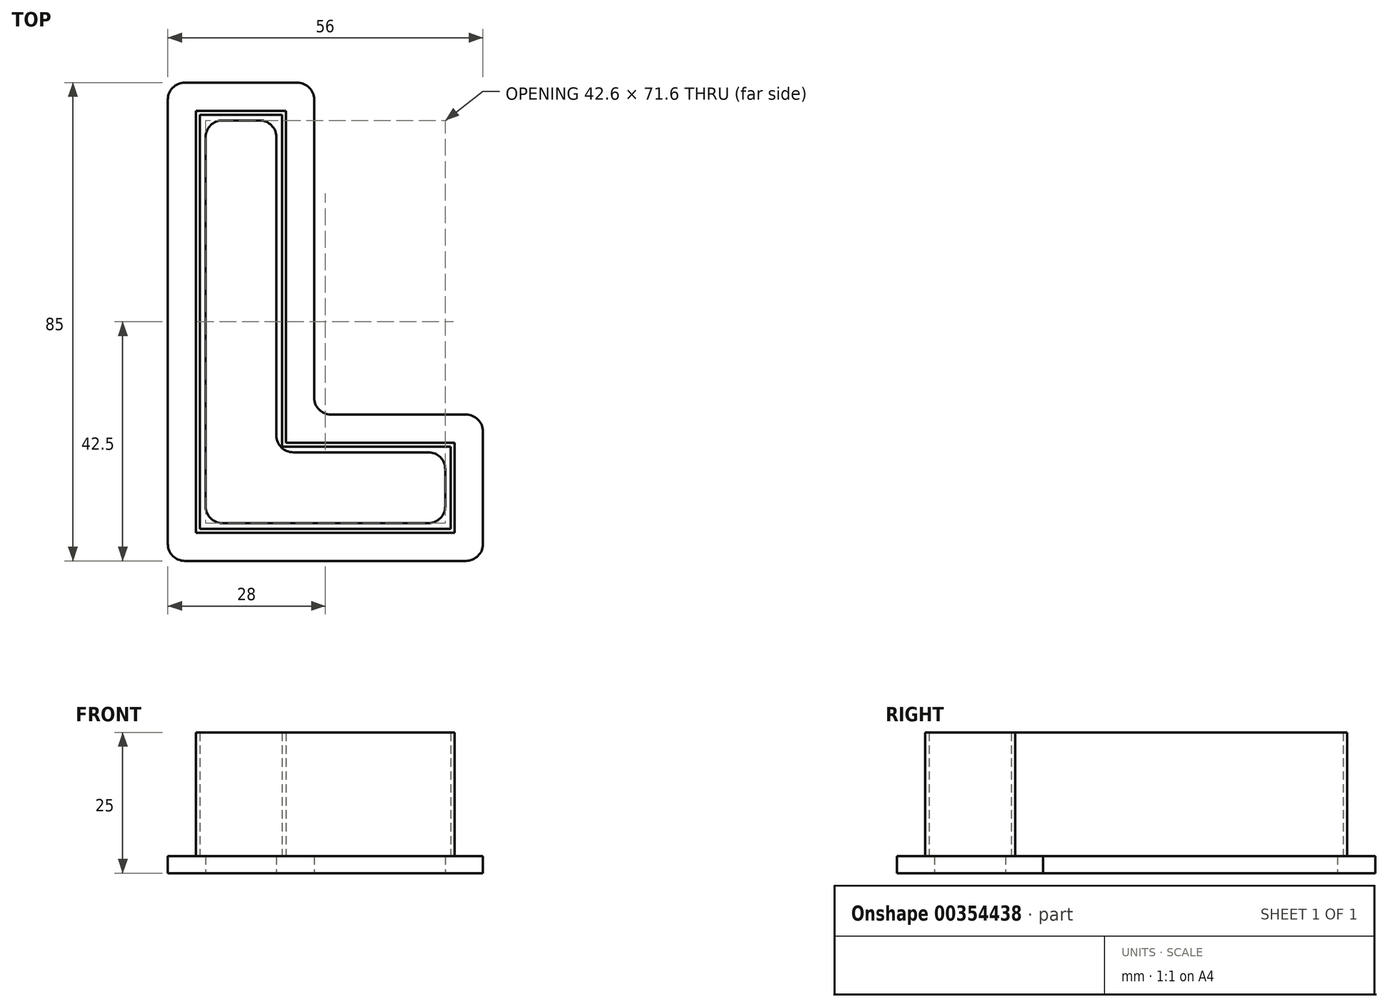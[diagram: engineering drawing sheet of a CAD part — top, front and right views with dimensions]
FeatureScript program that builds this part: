
annotation { "Feature Type Name" : "Feature", "Feature Type Description" : "" }
export const myFeature = defineFeature(function(context is Context, id is Id, definition is map)
    precondition{}
    {
        {
            var Q0;
            Q0=qCreatedBy(makeId("Top.planeOp"),FACE);
            var sketch = newSketch(context, id + "F0", { "sketchPlane" : qUnion([Q0])});
            skLineSegment(sketch, "E0", {"start": v(0, 0) * mm, "end": v(30, 0) * mm});
            skLineSegment(sketch, "E1", {"start": v(30, 0) * mm, "end": v(30, -16) * mm});
            skLineSegment(sketch, "E2", {"start": v(30, -16) * mm, "end": v(-16, -16) * mm});
            skLineSegment(sketch, "E3", {"start": v(-16, -16) * mm, "end": v(-16, 59) * mm});
            skLineSegment(sketch, "E4", {"start": v(-16, 59) * mm, "end": v(0, 59) * mm});
            skLineSegment(sketch, "E5", {"start": v(0, 59) * mm, "end": v(0, 0) * mm});
            skLineSegment(sketch, "E6.0", {"start": v(35, 5) * mm, "end": v(35, -21) * mm});
            skLineSegment(sketch, "E6.1", {"start": v(-21, -21) * mm, "end": v(-21, 64) * mm});
            skLineSegment(sketch, "E6.2", {"start": v(-21, 64) * mm, "end": v(5, 64) * mm});
            skLineSegment(sketch, "E6.3", {"start": v(35, -21) * mm, "end": v(-21, -21) * mm});
            skLineSegment(sketch, "E6.4", {"start": v(5, 64) * mm, "end": v(5, 5) * mm});
            skLineSegment(sketch, "E6.5", {"start": v(5, 5) * mm, "end": v(35, 5) * mm});
            skLineSegment(sketch, "E7.0", {"start": v(-0.7, 58.3) * mm, "end": v(-0.7, -0.7) * mm});
            skLineSegment(sketch, "E7.1", {"start": v(29.3, -0.7) * mm, "end": v(29.3, -15.3) * mm});
            skLineSegment(sketch, "E7.2", {"start": v(29.3, -15.3) * mm, "end": v(-15.3, -15.3) * mm});
            skLineSegment(sketch, "E7.3", {"start": v(-0.7, -0.7) * mm, "end": v(29.3, -0.7) * mm});
            skLineSegment(sketch, "E7.4", {"start": v(-15.3, -15.3) * mm, "end": v(-15.3, 58.3) * mm});
            skLineSegment(sketch, "E7.5", {"start": v(-15.3, 58.3) * mm, "end": v(-0.7, 58.3) * mm});
            skLineSegment(sketch, "E8.0", {"start": v(28.3, -14.3) * mm, "end": v(-14.3, -14.3) * mm});
            skLineSegment(sketch, "E8.1", {"start": v(-14.3, 57.3) * mm, "end": v(-1.7, 57.3) * mm});
            skLineSegment(sketch, "E8.2", {"start": v(-1.7, 57.3) * mm, "end": v(-1.7, -1.7) * mm});
            skLineSegment(sketch, "E8.3", {"start": v(-14.3, -14.3) * mm, "end": v(-14.3, 57.3) * mm});
            skLineSegment(sketch, "E8.4", {"start": v(-1.7, -1.7) * mm, "end": v(28.3, -1.7) * mm});
            skLineSegment(sketch, "E8.5", {"start": v(28.3, -1.7) * mm, "end": v(28.3, -14.3) * mm});
            skSolve(sketch);
        }
        {
            var Q0;
            Q0 = qSketchRegion(id + "F0", true);
            var Q1;
            Q1=makeQuery(id+"F0.imprint","IMPRINT",FACE,{"disambiguationData":[TD([[makeQuery(id+"F0.imprint","IMPRINT",EDGE,{"derivedFrom":sQuery(id+"F0.wireOp",EDGE,"E7.0")}),-1.0]])]});
            var Q2;
            Q2=makeQuery(id+"F0.imprint","IMPRINT",FACE,{"disambiguationData":[TD([[makeQuery(id+"F0.imprint","IMPRINT",EDGE,{"derivedFrom":sQuery(id+"F0.wireOp",EDGE,"E0")}),-1.0]])]});
            extrude(context, id + "F1", {"entities" : qUnion([Q0, Q1, Q2]), "depth" : 3 * mm});
        }
        {
            var Q0;
            Q0=makeQuery(id+"F0.imprint","IMPRINT",FACE,{"disambiguationData":[TD([[makeQuery(id+"F0.imprint","IMPRINT",EDGE,{"derivedFrom":sQuery(id+"F0.wireOp",EDGE,"E0")}),-1.0]])]});
            extrude(context, id + "F2", {"entities" : qUnion([Q0]), "operationType" : NewBodyOperationType.ADD, "depth" : 25 * mm});
        }
        {
            var Q0;
            Q0=makeQuery(id+"F1.opExtrude","SWEPT_EDGE",EDGE,{"disambiguationData":[OSD([sQuery(id+"F0.wireOp",EDGE,"E6.0"),sQuery(id+"F0.wireOp",EDGE,"E6.3")])]});
            var Q1;
            Q1=makeQuery(id+"F1.opExtrude","SWEPT_EDGE",EDGE,{"disambiguationData":[OSD([sQuery(id+"F0.wireOp",EDGE,"E6.0"),sQuery(id+"F0.wireOp",EDGE,"E6.5")])]});
            var Q2;
            Q2=makeQuery(id+"F1.opExtrude","SWEPT_EDGE",EDGE,{"disambiguationData":[OSD([sQuery(id+"F0.wireOp",EDGE,"E6.4"),sQuery(id+"F0.wireOp",EDGE,"E6.5")])]});
            var Q3;
            Q3=makeQuery(id+"F1.opExtrude","SWEPT_EDGE",EDGE,{"disambiguationData":[OSD([sQuery(id+"F0.wireOp",EDGE,"E6.2"),sQuery(id+"F0.wireOp",EDGE,"E6.4")])]});
            var Q4;
            Q4=makeQuery(id+"F1.opExtrude","SWEPT_EDGE",EDGE,{"disambiguationData":[OSD([sQuery(id+"F0.wireOp",EDGE,"E6.1"),sQuery(id+"F0.wireOp",EDGE,"E6.2")])]});
            var Q5;
            Q5=makeQuery(id+"F1.opExtrude","SWEPT_EDGE",EDGE,{"disambiguationData":[OSD([sQuery(id+"F0.wireOp",EDGE,"E6.1"),sQuery(id+"F0.wireOp",EDGE,"E6.3")])]});
            var Q6;
            Q6=makeQuery(id+"F1.opExtrude","SWEPT_EDGE",EDGE,{"disambiguationData":[OSD([sQuery(id+"F0.wireOp",EDGE,"E8.0"),sQuery(id+"F0.wireOp",EDGE,"E8.3")])]});
            var Q7;
            Q7=makeQuery(id+"F1.opExtrude","SWEPT_EDGE",EDGE,{"disambiguationData":[OSD([sQuery(id+"F0.wireOp",EDGE,"E8.2"),sQuery(id+"F0.wireOp",EDGE,"E8.4")])]});
            var Q8;
            Q8=makeQuery(id+"F1.opExtrude","SWEPT_EDGE",EDGE,{"disambiguationData":[OSD([sQuery(id+"F0.wireOp",EDGE,"E8.0"),sQuery(id+"F0.wireOp",EDGE,"E8.5")])]});
            var Q9;
            Q9=makeQuery(id+"F1.opExtrude","SWEPT_EDGE",EDGE,{"disambiguationData":[OSD([sQuery(id+"F0.wireOp",EDGE,"E8.4"),sQuery(id+"F0.wireOp",EDGE,"E8.5")])]});
            var Q10;
            Q10=makeQuery(id+"F1.opExtrude","SWEPT_EDGE",EDGE,{"disambiguationData":[OSD([sQuery(id+"F0.wireOp",EDGE,"E8.1"),sQuery(id+"F0.wireOp",EDGE,"E8.2")])]});
            var Q11;
            Q11=makeQuery(id+"F1.opExtrude","SWEPT_EDGE",EDGE,{"disambiguationData":[OSD([sQuery(id+"F0.wireOp",EDGE,"E8.1"),sQuery(id+"F0.wireOp",EDGE,"E8.3")])]});
            fillet(context, id + "F3", {"entities" : qUnion([Q0, Q1, Q2, Q3, Q4, Q5, Q6, Q7, Q8, Q9, Q10, Q11]), "radius" : 3 * mm, "tangentPropagation" : true, "allowEdgeOverflow" : false});
        }
    });
